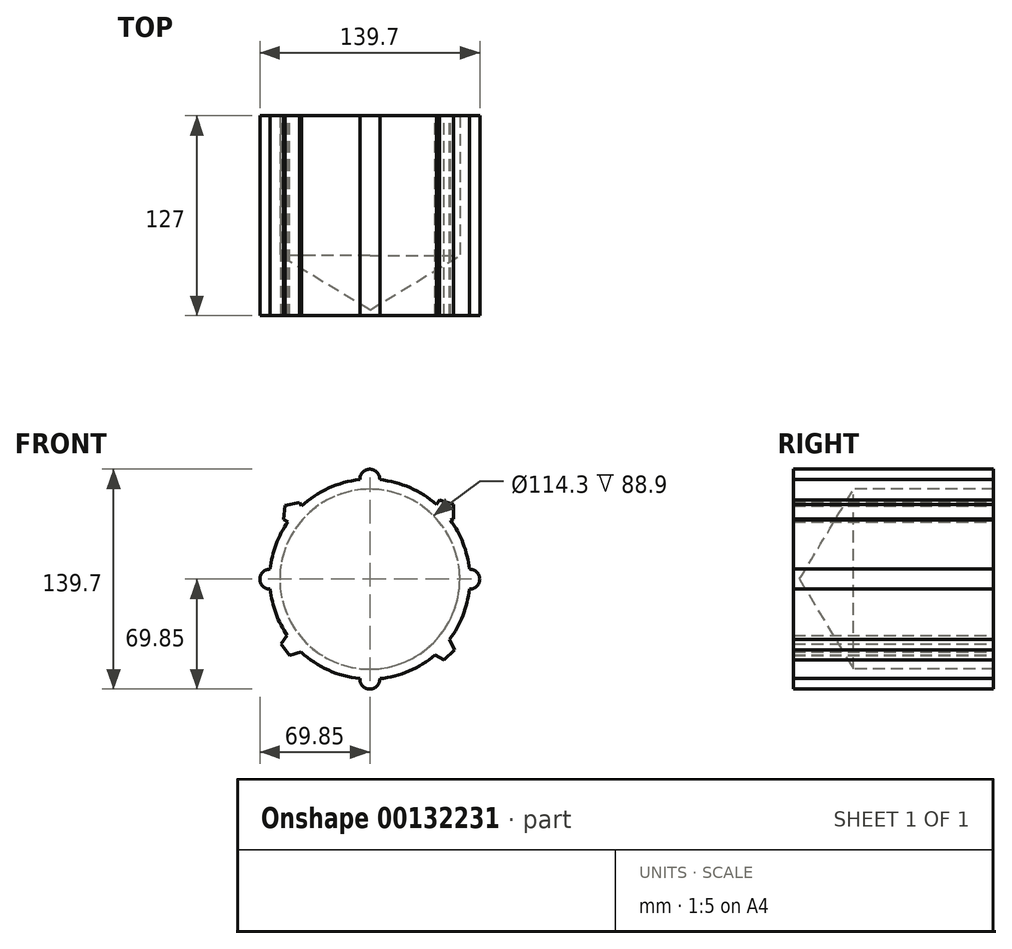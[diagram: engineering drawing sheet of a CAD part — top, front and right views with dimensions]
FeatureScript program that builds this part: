
annotation { "Feature Type Name" : "Feature", "Feature Type Description" : "" }
export const myFeature = defineFeature(function(context is Context, id is Id, definition is map)
    precondition{}
    {
        {
            var Q0;
            Q0=qCreatedBy(makeId("Front.planeOp"),FACE);
            var sketch = newSketch(context, id + "F0", { "sketchPlane" : qUnion([Q0])});
            skCircle(sketch, "E0", {"center": v(0, 0) * mm, "radius": 63.5 * mm});
            skCircle(sketch, "E1", {"center": v(-63.5, 0) * mm, "radius": 6.35 * mm});
            skCircle(sketch, "E2", {"center": v(63.5, 0) * mm, "radius": 6.35 * mm});
            skCircle(sketch, "E3", {"center": v(0, 63.5) * mm, "radius": 6.35 * mm});
            skCircle(sketch, "E4", {"center": v(0, -63.5) * mm, "radius": 6.35 * mm});
            skCircle(sketch, "E5.cCircle", {"center": v(-47.96, 41.62) * mm, "radius": 6.35 * mm, "construction": true});
            skLineSegment(sketch, "E5.0", {"start": v(-40.17, 40.65) * mm, "end": v(-46.47, 33.9) * mm});
            skLineSegment(sketch, "E5.1", {"start": v(-46.47, 33.9) * mm, "end": v(-54.83, 37.82) * mm});
            skLineSegment(sketch, "E5.2", {"start": v(-54.83, 37.82) * mm, "end": v(-53.7, 46.97) * mm});
            skLineSegment(sketch, "E5.3", {"start": v(-53.7, 46.97) * mm, "end": v(-44.64, 48.72) * mm});
            skLineSegment(sketch, "E5.4", {"start": v(-44.64, 48.72) * mm, "end": v(-40.17, 40.65) * mm});
            skPoint(sketch, "E5.0.midPoint", {"position": v(-43.32, 37.28) * mm});
            skCircle(sketch, "E6.cCircle", {"center": v(46.82, 42.9) * mm, "radius": 6.35 * mm, "construction": true});
            skLineSegment(sketch, "E6.0", {"start": v(53.17, 47.5) * mm, "end": v(53.17, 38.28) * mm});
            skLineSegment(sketch, "E6.1", {"start": v(53.17, 38.28) * mm, "end": v(44.4, 35.43) * mm});
            skLineSegment(sketch, "E6.2", {"start": v(44.4, 35.43) * mm, "end": v(38.97, 42.9) * mm});
            skLineSegment(sketch, "E6.3", {"start": v(38.97, 42.9) * mm, "end": v(44.4, 50.36) * mm});
            skLineSegment(sketch, "E6.4", {"start": v(44.4, 50.36) * mm, "end": v(53.17, 47.5) * mm});
            skPoint(sketch, "E6.0.midPoint", {"position": v(53.17, 42.9) * mm});
            skCircle(sketch, "E7.cCircle", {"center": v(46.22, -43.54) * mm, "radius": 6.35 * mm, "construction": true});
            skLineSegment(sketch, "E7.0", {"start": v(53.95, -44.93) * mm, "end": v(47.29, -51.32) * mm});
            skLineSegment(sketch, "E7.1", {"start": v(47.29, -51.32) * mm, "end": v(39.15, -46.96) * mm});
            skLineSegment(sketch, "E7.2", {"start": v(39.15, -46.96) * mm, "end": v(40.79, -37.88) * mm});
            skLineSegment(sketch, "E7.3", {"start": v(40.79, -37.88) * mm, "end": v(49.93, -36.62) * mm});
            skLineSegment(sketch, "E7.4", {"start": v(49.93, -36.62) * mm, "end": v(53.95, -44.93) * mm});
            skPoint(sketch, "E7.0.midPoint", {"position": v(50.62, -48.12) * mm});
            skPoint(sketch, "E8.0.midPoint", {"position": v(2.25, -2.76) * mm});
            skCircle(sketch, "E9.cCircle", {"center": v(-48.4, -41.1) * mm, "radius": 6.35 * mm, "construction": true});
            skLineSegment(sketch, "E9.0", {"start": v(-42.05, -36.5) * mm, "end": v(-42.05, -45.72) * mm});
            skLineSegment(sketch, "E9.1", {"start": v(-42.05, -45.72) * mm, "end": v(-50.82, -48.57) * mm});
            skLineSegment(sketch, "E9.2", {"start": v(-50.82, -48.57) * mm, "end": v(-56.25, -41.1) * mm});
            skLineSegment(sketch, "E9.3", {"start": v(-56.25, -41.1) * mm, "end": v(-50.82, -33.64) * mm});
            skLineSegment(sketch, "E9.4", {"start": v(-50.82, -33.64) * mm, "end": v(-42.05, -36.5) * mm});
            skPoint(sketch, "E9.0.midPoint", {"position": v(-42.05, -41.1) * mm});
            skSolve(sketch);
        }
        {
            var Q0;
            Q0 = qSketchRegion(id + "F0", true);
            extrude(context, id + "F1", {"entities" : qUnion([Q0]), "endBound" : BoundingType.SYMMETRIC, "depth" : 127 * mm});
        }
        {
            var Q0;
            Q0=sQuery(id+"F0.wireOp",VERTEX,"E0.center");
            var Q1;
            Q1=makeQuery(id+"F1.opExtrude","SWEPT_BODY",BODY,{"disambiguationData":[OSD([sQuery(id+"F0.wireOp",EDGE,"E0"),sQuery(id+"F0.wireOp",EDGE,"E1"),sQuery(id+"F0.wireOp",EDGE,"E2"),sQuery(id+"F0.wireOp",EDGE,"E3"),sQuery(id+"F0.wireOp",EDGE,"E4"),sQuery(id+"F0.wireOp",EDGE,"E5.1"),sQuery(id+"F0.wireOp",EDGE,"E5.2"),sQuery(id+"F0.wireOp",EDGE,"E5.3"),sQuery(id+"F0.wireOp",EDGE,"E5.4"),sQuery(id+"F0.wireOp",EDGE,"E6.0"),sQuery(id+"F0.wireOp",EDGE,"E6.1"),sQuery(id+"F0.wireOp",EDGE,"E6.3"),sQuery(id+"F0.wireOp",EDGE,"E6.4"),sQuery(id+"F0.wireOp",EDGE,"E7.0"),sQuery(id+"F0.wireOp",EDGE,"E7.1"),sQuery(id+"F0.wireOp",EDGE,"E7.4"),sQuery(id+"F0.wireOp",EDGE,"E9.1"),sQuery(id+"F0.wireOp",EDGE,"E9.2"),sQuery(id+"F0.wireOp",EDGE,"E9.3")])]});
            hole(context, id + "F2", {"style" : HoleStyle.SIMPLE, "endStyle" : HoleEndStyle.THROUGH, "holeDiameter" : 114.3 * mm, "locations" : qUnion([Q0]), "scope" : qUnion([Q1]), "isTappedThrough" : true});
        }
        {
            var Q0;
            Q0=sQuery(id+"F0.wireOp",VERTEX,"E0.center");
            var Q1;
            Q1=makeQuery(id+"F1.opExtrude","SWEPT_BODY",BODY,{"disambiguationData":[OSD([sQuery(id+"F0.wireOp",EDGE,"E0"),sQuery(id+"F0.wireOp",EDGE,"E1"),sQuery(id+"F0.wireOp",EDGE,"E2"),sQuery(id+"F0.wireOp",EDGE,"E3"),sQuery(id+"F0.wireOp",EDGE,"E4"),sQuery(id+"F0.wireOp",EDGE,"E5.1"),sQuery(id+"F0.wireOp",EDGE,"E5.2"),sQuery(id+"F0.wireOp",EDGE,"E5.3"),sQuery(id+"F0.wireOp",EDGE,"E5.4"),sQuery(id+"F0.wireOp",EDGE,"E6.0"),sQuery(id+"F0.wireOp",EDGE,"E6.1"),sQuery(id+"F0.wireOp",EDGE,"E6.3"),sQuery(id+"F0.wireOp",EDGE,"E6.4"),sQuery(id+"F0.wireOp",EDGE,"E7.0"),sQuery(id+"F0.wireOp",EDGE,"E7.1"),sQuery(id+"F0.wireOp",EDGE,"E7.4"),sQuery(id+"F0.wireOp",EDGE,"E9.1"),sQuery(id+"F0.wireOp",EDGE,"E9.2"),sQuery(id+"F0.wireOp",EDGE,"E9.3")])]});
            hole(context, id + "F3", {"style" : HoleStyle.SIMPLE, "endStyle" : HoleEndStyle.BLIND, "oppositeDirection" : true, "holeDiameter" : 114.3 * mm, "holeDepth" : 25.4 * mm, "locations" : qUnion([Q0]), "scope" : qUnion([Q1])});
        }
    });
